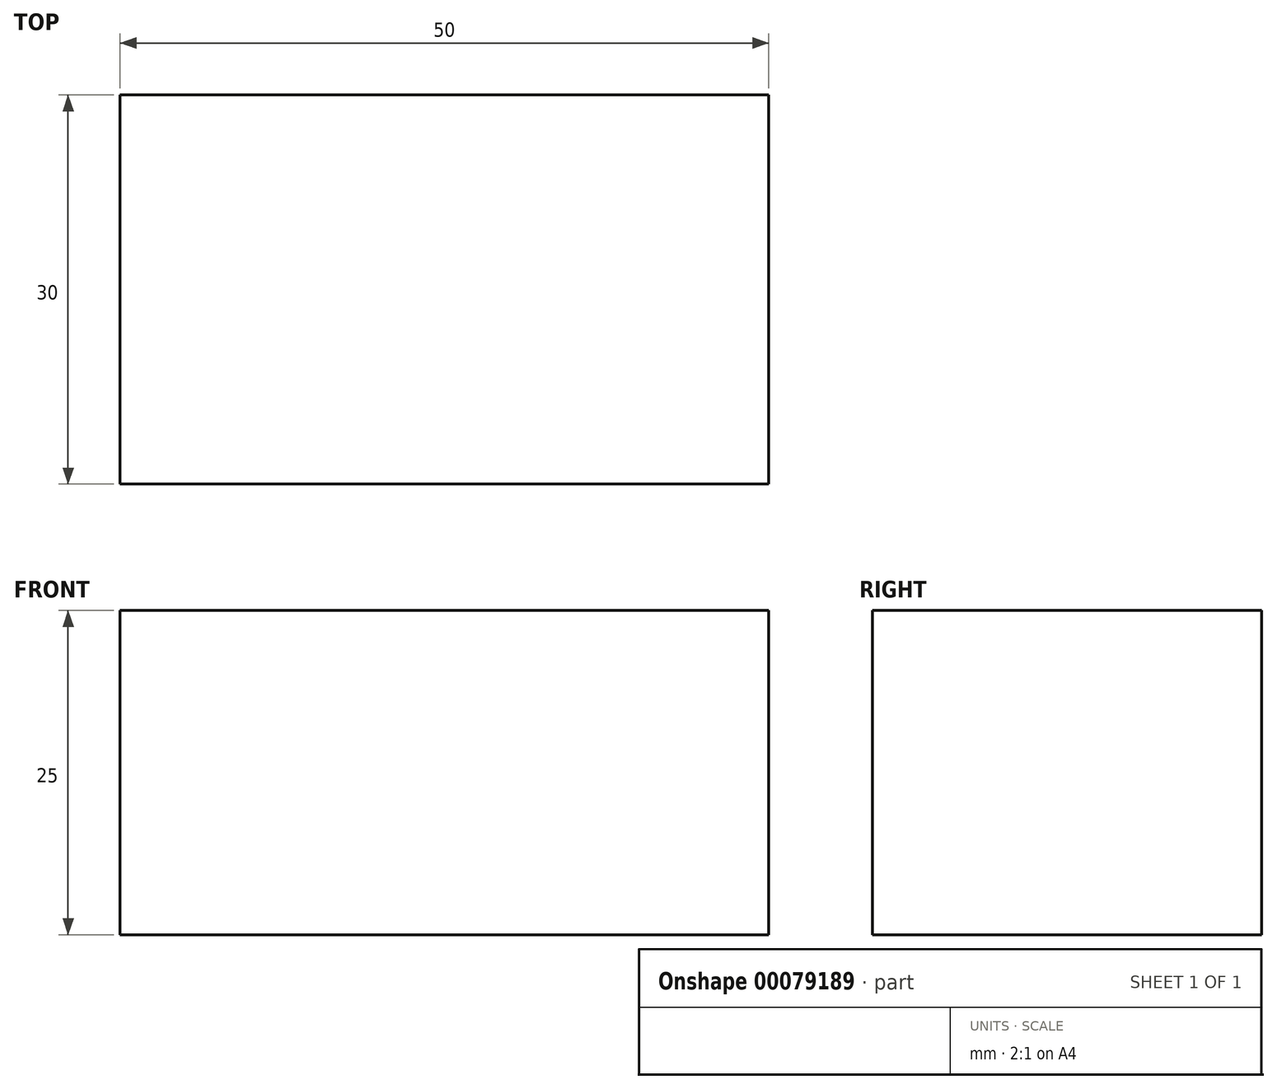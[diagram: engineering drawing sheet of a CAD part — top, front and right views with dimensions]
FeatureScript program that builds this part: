
annotation { "Feature Type Name" : "Feature", "Feature Type Description" : "" }
export const myFeature = defineFeature(function(context is Context, id is Id, definition is map)
    precondition{}
    {
        {
            var Q0;
            Q0=qCreatedBy(makeId("Top.planeOp"),FACE);
            var sketch = newSketch(context, id + "F0", { "sketchPlane" : qUnion([Q0])});
            skLineSegment(sketch, "E0.bottom", {"start": v(0, 0) * mm, "end": v(50, 0) * mm});
            skLineSegment(sketch, "E0.top", {"start": v(0, 30) * mm, "end": v(50, 30) * mm});
            skLineSegment(sketch, "E0.left", {"start": v(0, 0) * mm, "end": v(0, 30) * mm});
            skLineSegment(sketch, "E0.right", {"start": v(50, 0) * mm, "end": v(50, 30) * mm});
            skSolve(sketch);
        }
        {
            var Q0;
            Q0 = qSketchRegion(id + "F0", true);
            extrude(context, id + "F1", {"entities" : qUnion([Q0]), "depth" : 25 * mm, "offsetDistance" : 25 * mm});
        }
    });
